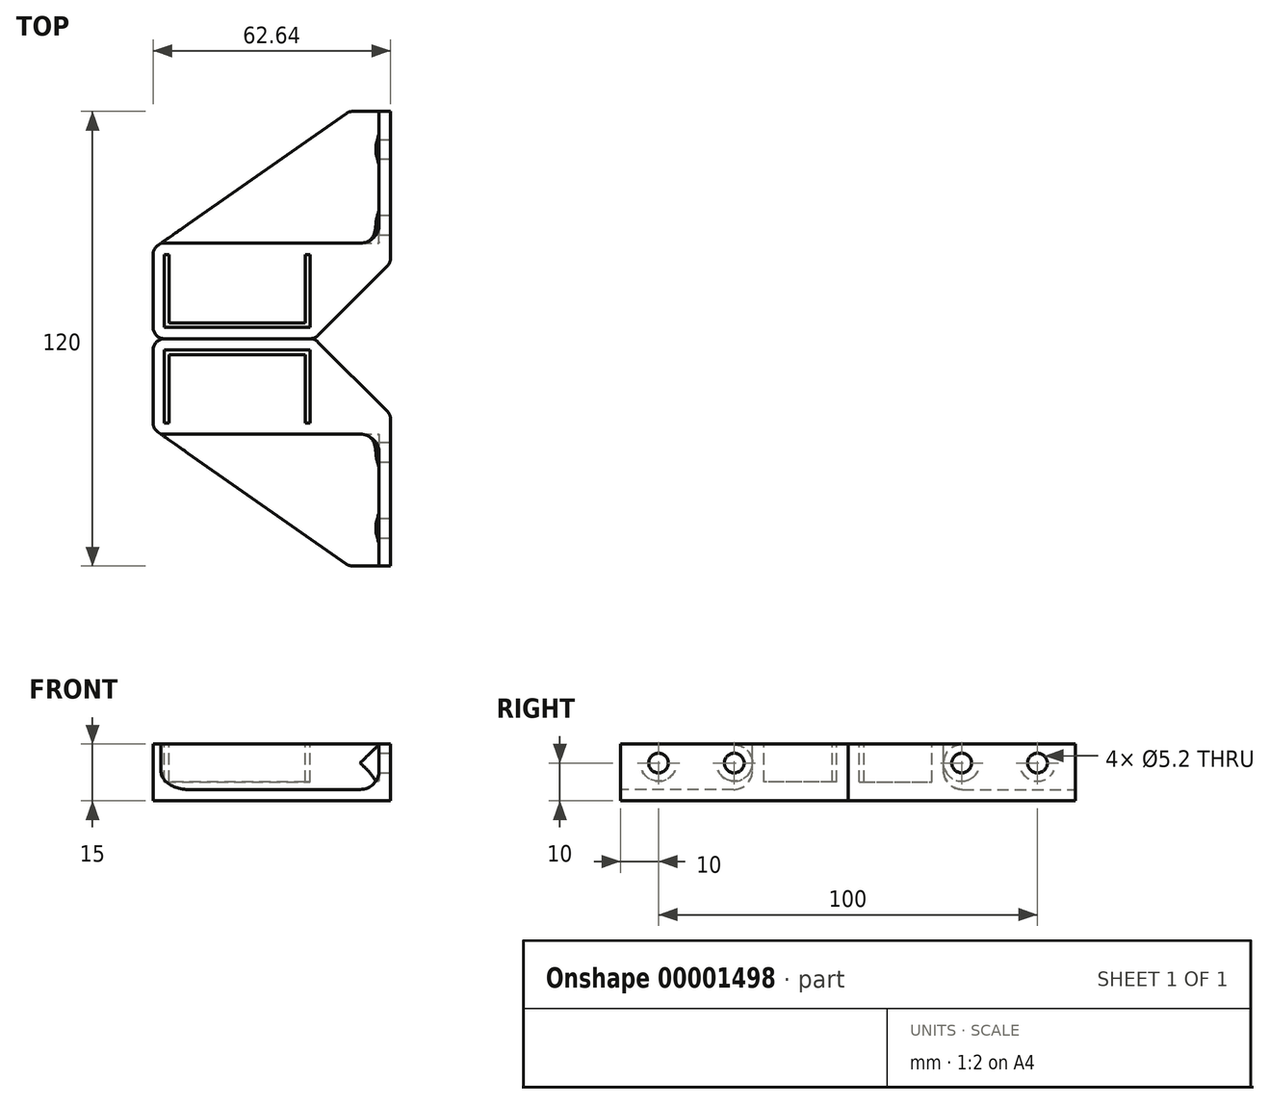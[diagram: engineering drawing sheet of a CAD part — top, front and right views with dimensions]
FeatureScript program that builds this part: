
annotation { "Feature Type Name" : "Feature", "Feature Type Description" : "" }
export const myFeature = defineFeature(function(context is Context, id is Id, definition is map)
    precondition{}
    {
        {
            var Q0;
            Q0=qCreatedBy(makeId("Front.planeOp"),FACE);
            var sketch = newSketch(context, id + "F0", { "sketchPlane" : qUnion([Q0])});
            skLineSegment(sketch, "E0", {"start": v(-19.12, 0.88) * mm, "end": v(-0.88, 19.12) * mm});
            skLineSegment(sketch, "E1", {"start": v(0, 21.24) * mm, "end": v(0, 60) * mm});
            skLineSegment(sketch, "E2", {"start": v(0, 60) * mm, "end": v(-10, 60) * mm});
            skLineSegment(sketch, "E3", {"start": v(-11.72, 59.46) * mm, "end": v(-61.36, 24.66) * mm});
            skLineSegment(sketch, "E4", {"start": v(-62.64, 22.2) * mm, "end": v(-62.64, 3) * mm});
            skLineSegment(sketch, "E5", {"start": v(-59.64, 0) * mm, "end": v(-21.24, 0) * mm});
            skPoint(sketch, "E6.visualSharp", {"position": v(0, 60) * mm});
            skPoint(sketch, "E7.visualSharp", {"position": v(-10.95, 60) * mm});
            skArc(sketch, "E7.filletArc", {"start": v(-10, 60) * mm, "mid": v(-10.9, 59.86) * mm, "end": v(-11.72, 59.46) * mm});
            skPoint(sketch, "E8.visualSharp", {"position": v(-62.64, 23.76) * mm});
            skArc(sketch, "E8.filletArc", {"start": v(-61.36, 24.66) * mm, "mid": v(-62.3, 23.58) * mm, "end": v(-62.64, 22.2) * mm});
            skPoint(sketch, "E9.visualSharp", {"position": v(-62.64, 0) * mm});
            skArc(sketch, "E9.filletArc", {"start": v(-62.64, 3) * mm, "mid": v(-61.76, 0.88) * mm, "end": v(-59.64, 0) * mm});
            skPoint(sketch, "E10.visualSharp", {"position": v(-20, 0) * mm});
            skArc(sketch, "E10.filletArc", {"start": v(-21.24, 0) * mm, "mid": v(-20.1, 0.23) * mm, "end": v(-19.12, 0.88) * mm});
            skPoint(sketch, "E11.visualSharp", {"position": v(0, 20) * mm});
            skArc(sketch, "E11.filletArc", {"start": v(-0.88, 19.12) * mm, "mid": v(-0.23, 20.1) * mm, "end": v(0, 21.24) * mm});
            skSolve(sketch);
        }
        {
            var Q0;
            Q0=makeQuery(id+"F0.imprint","IMPRINT",FACE,{"disambiguationData":[TD([[makeQuery(id+"F0.imprint","IMPRINT",EDGE,{"derivedFrom":sQuery(id+"F0.wireOp",EDGE,"E0")}),1.0]])]});
            extrude(context, id + "F1", {"entities" : qUnion([Q0]), "depth" : 15 * mm});
        }
        {
            var Q0;
            Q0=makeQuery(id+"F1.opExtrude","CAP_FACE",FACE,{"disambiguationData":[OSD([sQuery(id+"F0.wireOp",EDGE,"E0"),sQuery(id+"F0.wireOp",EDGE,"E1"),sQuery(id+"F0.wireOp",EDGE,"E2"),sQuery(id+"F0.wireOp",EDGE,"E3"),sQuery(id+"F0.wireOp",EDGE,"E4"),sQuery(id+"F0.wireOp",EDGE,"E5"),sQuery(id+"F0.wireOp",EDGE,"E7.filletArc"),sQuery(id+"F0.wireOp",EDGE,"E8.filletArc"),sQuery(id+"F0.wireOp",EDGE,"E9.filletArc"),sQuery(id+"F0.wireOp",EDGE,"E10.filletArc"),sQuery(id+"F0.wireOp",EDGE,"E11.filletArc")])],"isStart":true});
            var sketch = newSketch(context, id + "F2", { "sketchPlane" : qUnion([Q0])});
            skLineSegment(sketch, "E12", {"start": v(21.24, 3) * mm, "end": v(21.24, 22.2) * mm});
            skLineSegment(sketch, "E13", {"start": v(21.24, 22.2) * mm, "end": v(22.44, 22.2) * mm});
            skLineSegment(sketch, "E14", {"start": v(22.44, 22.2) * mm, "end": v(22.44, 4.2) * mm});
            skLineSegment(sketch, "E15", {"start": v(22.44, 4.2) * mm, "end": v(58.44, 4.2) * mm});
            skLineSegment(sketch, "E16", {"start": v(58.44, 4.2) * mm, "end": v(58.44, 22.2) * mm});
            skLineSegment(sketch, "E17", {"start": v(58.44, 22.2) * mm, "end": v(59.64, 22.2) * mm});
            skLineSegment(sketch, "E18", {"start": v(59.64, 22.2) * mm, "end": v(59.64, 3) * mm});
            skLineSegment(sketch, "E19", {"start": v(59.64, 3) * mm, "end": v(21.24, 3) * mm});
            skSolve(sketch);
        }
        {
            var Q0;
            Q0=makeQuery(id+"F2.imprint","IMPRINT",FACE,{"disambiguationData":[TD([[makeQuery(id+"F2.imprint","IMPRINT",EDGE,{"derivedFrom":sQuery(id+"F2.wireOp",EDGE,"E12")}),-1.0]])]});
            extrude(context, id + "F3", {"entities" : qUnion([Q0]), "operationType" : NewBodyOperationType.REMOVE, "oppositeDirection" : true, "depth" : 10 * mm});
        }
        {
            var Q0;
            Q0=makeQuery(id+"F1.opExtrude","CAP_FACE",FACE,{"disambiguationData":[OSD([sQuery(id+"F0.wireOp",EDGE,"E0"),sQuery(id+"F0.wireOp",EDGE,"E1"),sQuery(id+"F0.wireOp",EDGE,"E2"),sQuery(id+"F0.wireOp",EDGE,"E3"),sQuery(id+"F0.wireOp",EDGE,"E4"),sQuery(id+"F0.wireOp",EDGE,"E5"),sQuery(id+"F0.wireOp",EDGE,"E7.filletArc"),sQuery(id+"F0.wireOp",EDGE,"E8.filletArc"),sQuery(id+"F0.wireOp",EDGE,"E9.filletArc"),sQuery(id+"F0.wireOp",EDGE,"E10.filletArc"),sQuery(id+"F0.wireOp",EDGE,"E11.filletArc")])],"isStart":true});
            var sketch = newSketch(context, id + "F4", { "sketchPlane" : qUnion([Q0])});
            skLineSegment(sketch, "E20.bottom", {"start": v(3, 25.2) * mm, "end": v(63, 25.2) * mm});
            skLineSegment(sketch, "E20.top", {"start": v(3, 60) * mm, "end": v(63, 60) * mm});
            skLineSegment(sketch, "E20.left", {"start": v(3, 25.2) * mm, "end": v(3, 60) * mm});
            skLineSegment(sketch, "E20.right", {"start": v(63, 25.2) * mm, "end": v(63, 60) * mm});
            skSolve(sketch);
        }
        {
            var Q0;
            {var subQ6=sQuery(id+"F4.wireOp",EDGE,"E20.right");var subQ9=sQuery(id+"F4.wireOp",EDGE,"E20.left");Q0=qUnion([makeQuery(id+"F4.imprint","IMPRINT",FACE,{"disambiguationData":[TD([[makeQuery(id+"F4.imprint","IMPRINT",EDGE,{"derivedFrom":subQ6}),1.0]])]}),makeQuery(id+"F4.imprint","IMPRINT",FACE,{"disambiguationData":[TD([[makeQuery(id+"F4.imprint","IMPRINT",EDGE,{"derivedFrom":subQ9}),-1.0]])]})]);}
            extrude(context, id + "F5", {"entities" : qUnion([Q0]), "operationType" : NewBodyOperationType.REMOVE, "oppositeDirection" : true, "depth" : 12 * mm});
        }
        {
            var Q0;
            Q0=makeQuery(id+"F5.boolean.opBoolean","COPY",EDGE,{"derivedFrom":makeQuery(id+"F5.opExtrude","CAP_EDGE",EDGE,{"disambiguationData":[OSD([sQuery(id+"F4.wireOp",EDGE,"E20.left")])],"isStart":false})});
            var Q1;
            Q1=makeQuery(id+"F5.boolean.opBoolean","COPY",EDGE,{"derivedFrom":makeQuery(id+"F5.opExtrude","CAP_EDGE",EDGE,{"disambiguationData":[OSD([sQuery(id+"F4.wireOp",EDGE,"E20.bottom")])],"isStart":false})});
            var Q2;
            Q2=makeQuery(id+"F5.boolean.opBoolean","COPY",EDGE,{"derivedFrom":makeQuery(id+"F5.opExtrude","SWEPT_EDGE",EDGE,{"disambiguationData":[OSD([sQuery(id+"F4.wireOp",EDGE,"E20.bottom"),sQuery(id+"F4.wireOp",EDGE,"E20.left")])]})});
            fillet(context, id + "F6", {"entities" : qUnion([Q0, Q1, Q2]), "radius" : 5 * mm, "tangentPropagation" : true, "allowEdgeOverflow" : false});
        }
        {
            var Q0;
            Q0=makeQuery(id+"F1.opExtrude","SWEPT_FACE",FACE,{"disambiguationData":[OSD([sQuery(id+"F0.wireOp",EDGE,"E1")])]});
            var sketch = newSketch(context, id + "F7", { "sketchPlane" : qUnion([Q0])});
            skCircle(sketch, "E21", {"center": v(-5, 50) * mm, "radius": 2.6 * mm});
            skCircle(sketch, "E22", {"center": v(-5, 30) * mm, "radius": 2.6 * mm});
            skSolve(sketch);
        }
        {
            var Q0;
            {Q0=qUnion([makeQuery(id+"F7.imprint","IMPRINT",FACE,{"disambiguationData":[TD([[makeQuery(id+"F7.imprint","IMPRINT",EDGE,{"derivedFrom":sQuery(id+"F7.wireOp",EDGE,"E21")}),1.0]])]}),makeQuery(id+"F7.imprint","IMPRINT",FACE,{"disambiguationData":[TD([[makeQuery(id+"F7.imprint","IMPRINT",EDGE,{"derivedFrom":sQuery(id+"F7.wireOp",EDGE,"E22")}),1.0]])]})]);}
            extrude(context, id + "F8", {"entities" : qUnion([Q0]), "operationType" : NewBodyOperationType.REMOVE, "endBound" : BoundingType.THROUGH_ALL, "oppositeDirection" : true, "depth" : 25 * mm});
        }
        {
            var Q0;
            Q0=makeQuery(id+"F5.boolean.opBoolean","COPY",FACE,{"derivedFrom":makeQuery(id+"F5.opExtrude","SWEPT_FACE",FACE,{"disambiguationData":[OSD([sQuery(id+"F4.wireOp",EDGE,"E20.left")])]})});
            var sketch = newSketch(context, id + "F9", { "sketchPlane" : qUnion([Q0])});
            skCircle(sketch, "E23", {"center": v(5, 50) * mm, "radius": 4.8 * mm});
            skCircle(sketch, "E24", {"center": v(5, 30) * mm, "radius": 4.8 * mm});
            skSolve(sketch);
        }
        {
            var Q0;
            {var subQ0=sQuery(id+"F4.wireOp",EDGE,"E20.left");var subQ1=makeQuery(id+"F5.boolean.opBoolean","COPY",FACE,{"derivedFrom":makeQuery(id+"F5.opExtrude","SWEPT_FACE",FACE,{"disambiguationData":[OSD([subQ0])]})});var subQ3=makeQuery(id+"F8.opExtrude","SWEPT_FACE",FACE,{"disambiguationData":[OSD([sQuery(id+"F7.wireOp",EDGE,"E22")])]});var subQ4=makeQuery(id+"F8.opExtrude","SWEPT_FACE",FACE,{"disambiguationData":[OSD([sQuery(id+"F7.wireOp",EDGE,"E21")])]});var subQ9=subQ1;var subQ10=makeQuery(id+"F8.boolean.opBoolean","INTERSECT",EDGE,{"derivedFrom":[subQ9,subQ4]});var subQ15=makeQuery(id+"F9.imprint","IMPRINT",EDGE,{"derivedFrom":subQ10});var subQ19=makeQuery(id+"F8.boolean.opBoolean","INTERSECT",EDGE,{"derivedFrom":[subQ9,subQ3]});var subQ23=makeQuery(id+"F9.imprint","IMPRINT",EDGE,{"derivedFrom":subQ19});Q0=qUnion([makeQuery(id+"F9.imprint","IMPRINT",FACE,{"disambiguationData":[TD([[subQ15,1.0]])]}),makeQuery(id+"F9.imprint","IMPRINT",FACE,{"disambiguationData":[TD([[subQ23,1.0]])]}),makeQuery(id+"F9.imprint","IMPRINT",FACE,{"disambiguationData":[TD([[subQ15,-1.0]])]}),makeQuery(id+"F9.imprint","IMPRINT",FACE,{"disambiguationData":[TD([[subQ23,-1.0]])]})]);}
            extrude(context, id + "F10", {"entities" : qUnion([Q0]), "operationType" : NewBodyOperationType.REMOVE, "depth" : 10 * mm});
        }
        {
            var Q0;
            Q0=makeQuery(id+"F1.opExtrude","SWEPT_BODY",BODY,{"disambiguationData":[OSD([sQuery(id+"F0.wireOp",EDGE,"E0"),sQuery(id+"F0.wireOp",EDGE,"E1"),sQuery(id+"F0.wireOp",EDGE,"E2"),sQuery(id+"F0.wireOp",EDGE,"E3"),sQuery(id+"F0.wireOp",EDGE,"E4"),sQuery(id+"F0.wireOp",EDGE,"E5"),sQuery(id+"F0.wireOp",EDGE,"E7.filletArc"),sQuery(id+"F0.wireOp",EDGE,"E8.filletArc"),sQuery(id+"F0.wireOp",EDGE,"E9.filletArc"),sQuery(id+"F0.wireOp",EDGE,"E10.filletArc"),sQuery(id+"F0.wireOp",EDGE,"E11.filletArc")])]});
            var Q1;
            Q1=qCreatedBy(makeId("Front.planeOp"),FACE);
            mirror(context, id + "F11", {"entities" : qUnion([Q0]), "mirrorPlane" : qUnion([Q1])});
        }
        {
            var Q0;
            Q0=makeQuery(id+"F11.opPattern","COPY",BODY,{"derivedFrom":makeQuery(id+"F1.opExtrude","SWEPT_BODY",BODY,{"disambiguationData":[OSD([sQuery(id+"F0.wireOp",EDGE,"E0"),sQuery(id+"F0.wireOp",EDGE,"E1"),sQuery(id+"F0.wireOp",EDGE,"E2"),sQuery(id+"F0.wireOp",EDGE,"E3"),sQuery(id+"F0.wireOp",EDGE,"E4"),sQuery(id+"F0.wireOp",EDGE,"E5"),sQuery(id+"F0.wireOp",EDGE,"E7.filletArc"),sQuery(id+"F0.wireOp",EDGE,"E8.filletArc"),sQuery(id+"F0.wireOp",EDGE,"E9.filletArc"),sQuery(id+"F0.wireOp",EDGE,"E10.filletArc"),sQuery(id+"F0.wireOp",EDGE,"E11.filletArc")])]}),"instanceName":"1"});
            var Q1;
            Q1=makeQuery(id+"F1.opExtrude","CAP_EDGE",EDGE,{"disambiguationData":[OSD([sQuery(id+"F0.wireOp",EDGE,"E5")])],"isStart":true});
            transform(context, id + "F12", {"entities" : qUnion([Q0]), "transformType" : TransformType.ROTATION, "transformAxis" : qUnion([Q1]), "angle" : 270 * degree, "makeCopy" : false});
        }
        {
            var Q0;
            Q0=makeQuery(id+"F1.opExtrude","SWEPT_BODY",BODY,{"disambiguationData":[OSD([sQuery(id+"F0.wireOp",EDGE,"E0"),sQuery(id+"F0.wireOp",EDGE,"E1"),sQuery(id+"F0.wireOp",EDGE,"E2"),sQuery(id+"F0.wireOp",EDGE,"E3"),sQuery(id+"F0.wireOp",EDGE,"E4"),sQuery(id+"F0.wireOp",EDGE,"E5"),sQuery(id+"F0.wireOp",EDGE,"E7.filletArc"),sQuery(id+"F0.wireOp",EDGE,"E8.filletArc"),sQuery(id+"F0.wireOp",EDGE,"E9.filletArc"),sQuery(id+"F0.wireOp",EDGE,"E10.filletArc"),sQuery(id+"F0.wireOp",EDGE,"E11.filletArc")])]});
            var Q1;
            Q1=makeQuery(id+"F1.opExtrude","CAP_EDGE",EDGE,{"disambiguationData":[OSD([sQuery(id+"F0.wireOp",EDGE,"E5")])],"isStart":true});
            transform(context, id + "F13", {"entities" : qUnion([Q0]), "transformType" : TransformType.ROTATION, "transformAxis" : qUnion([Q1]), "angle" : 90 * degree, "makeCopy" : false});
        }
    });
